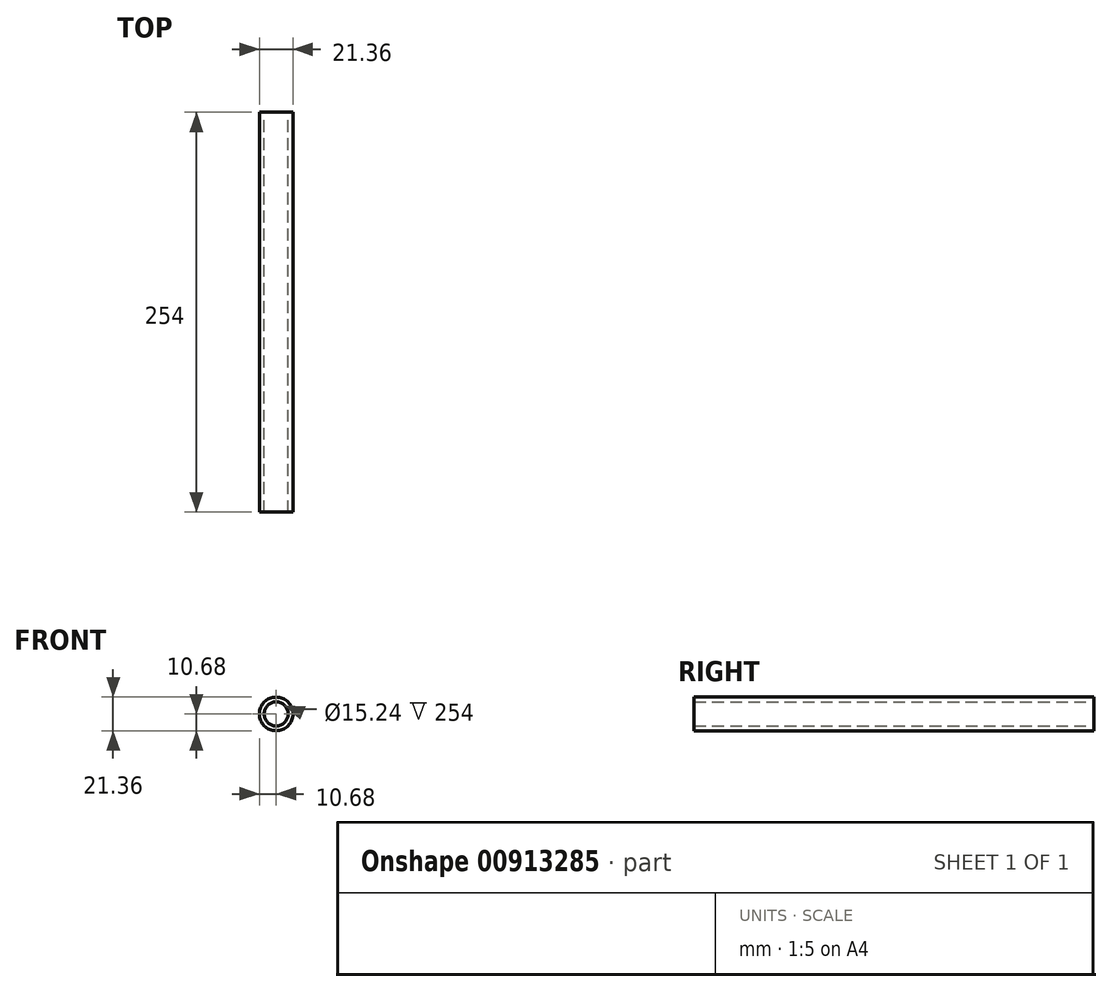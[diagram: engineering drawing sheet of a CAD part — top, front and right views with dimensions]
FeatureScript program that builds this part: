
annotation { "Feature Type Name" : "Feature", "Feature Type Description" : "" }
export const myFeature = defineFeature(function(context is Context, id is Id, definition is map)
    precondition{}
    {
        {
            var Q0;
            Q0=qCreatedBy(makeId("Front.planeOp"),FACE);
            var sketch = newSketch(context, id + "F0", { "sketchPlane" : qUnion([Q0])});
            skCircle(sketch, "E0", {"center": v(0, 0) * mm, "radius": 10.68 * mm});
            skCircle(sketch, "E1", {"center": v(0, 0) * mm, "radius": 7.62 * mm});
            skSolve(sketch);
        }
        {
            var Q0;
            Q0=makeQuery(id+"F0.imprint","IMPRINT",FACE,{"disambiguationData":[TD([[makeQuery(id+"F0.imprint","IMPRINT",EDGE,{"derivedFrom":sQuery(id+"F0.wireOp",EDGE,"E0")}),1.0]])]});
            extrude(context, id + "F1", {"entities" : qUnion([Q0]), "depth" : 254 * mm, "offsetDistance" : 25.4 * mm});
        }
    });
